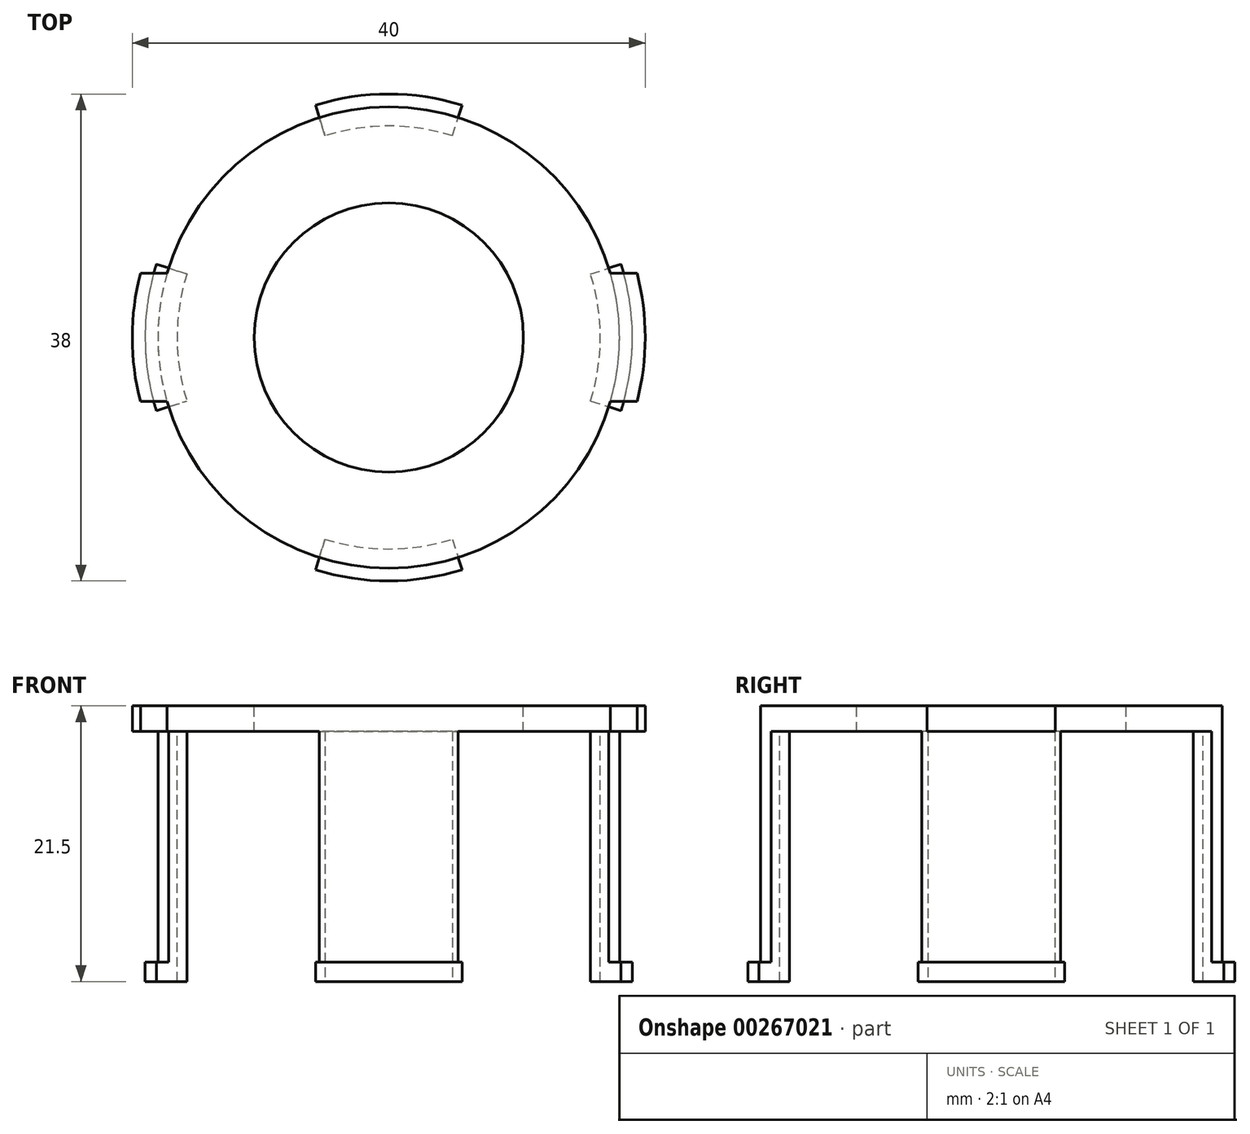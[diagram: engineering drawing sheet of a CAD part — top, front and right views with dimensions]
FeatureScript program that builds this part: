
annotation { "Feature Type Name" : "Feature", "Feature Type Description" : "" }
export const myFeature = defineFeature(function(context is Context, id is Id, definition is map)
    precondition{}
    {
        {
            var Q0;
            Q0=qCreatedBy(makeId("Top.planeOp"),FACE);
            var sketch = newSketch(context, id + "F0", { "sketchPlane" : qUnion([Q0])});
            skCircle(sketch, "E0", {"center": v(0, 0) * mm, "radius": 16.5 * mm});
            skCircle(sketch, "E1", {"center": v(0, 0) * mm, "radius": 18 * mm});
            skSolve(sketch);
        }
        {
            var Q0;
            Q0 = qSketchRegion(id + "F0", true);
            extrude(context, id + "F1", {"entities" : qUnion([Q0]), "oppositeDirection" : true, "depth" : 20 * mm});
        }
        {
            var Q0;
            Q0=makeQuery(id+"F1.opExtrude","CAP_FACE",FACE,{"disambiguationData":[OSD([sQuery(id+"F0.wireOp",EDGE,"E0"),sQuery(id+"F0.wireOp",EDGE,"E1")])],"isStart":false});
            var sketch = newSketch(context, id + "F2", { "sketchPlane" : qUnion([Q0])});
            skLineSegment(sketch, "E2", {"start": v(-17.17, 5.41) * mm, "end": v(-15.74, 4.96) * mm});
            skLineSegment(sketch, "E3", {"start": v(-17.17, -5.41) * mm, "end": v(-15.74, -4.96) * mm});
            skLineSegment(sketch, "E4", {"start": v(-5.41, 17.17) * mm, "end": v(-4.96, 15.74) * mm});
            skLineSegment(sketch, "E5", {"start": v(-5.41, -17.17) * mm, "end": v(-4.96, -15.74) * mm});
            skArc(sketch, "E6", {"start": v(-17.17, -5.41) * mm, "mid": v(-12.73, -12.73) * mm, "end": v(-5.41, -17.17) * mm});
            skArc(sketch, "E7", {"start": v(-15.74, -4.96) * mm, "mid": v(-11.67, -11.67) * mm, "end": v(-4.96, -15.74) * mm});
            skLineSegment(sketch, "E8.trimOffspring", {"start": v(4.96, -15.74) * mm, "end": v(5.41, -17.17) * mm});
            skLineSegment(sketch, "E9.trimOffspring", {"start": v(4.96, 15.74) * mm, "end": v(5.41, 17.17) * mm});
            skLineSegment(sketch, "E10.trimOffspring", {"start": v(15.74, 4.96) * mm, "end": v(17.17, 5.41) * mm});
            skLineSegment(sketch, "E11.trimOffspring", {"start": v(15.74, -4.96) * mm, "end": v(17.17, -5.41) * mm});
            skArc(sketch, "E12.trimOffspring", {"start": v(5.41, -17.17) * mm, "mid": v(12.73, -12.73) * mm, "end": v(17.17, -5.41) * mm});
            skArc(sketch, "E13.trimOffspring", {"start": v(4.96, -15.74) * mm, "mid": v(11.67, -11.67) * mm, "end": v(15.74, -4.96) * mm});
            skArc(sketch, "E14.trimOffspring", {"start": v(15.74, 4.96) * mm, "mid": v(11.67, 11.67) * mm, "end": v(4.96, 15.74) * mm});
            skArc(sketch, "E15.trimOffspring", {"start": v(17.17, 5.41) * mm, "mid": v(12.73, 12.73) * mm, "end": v(5.41, 17.17) * mm});
            skArc(sketch, "E16.trimOffspring", {"start": v(-5.41, 17.17) * mm, "mid": v(-12.73, 12.73) * mm, "end": v(-17.17, 5.41) * mm});
            skArc(sketch, "E17.trimOffspring", {"start": v(-4.96, 15.74) * mm, "mid": v(-11.67, 11.67) * mm, "end": v(-15.74, 4.96) * mm});
            skSolve(sketch);
        }
        {
            var Q0;
            Q0 = qSketchRegion(id + "F2", true);
            extrude(context, id + "F3", {"entities" : qUnion([Q0]), "operationType" : NewBodyOperationType.REMOVE, "oppositeDirection" : true, "depth" : 18 * mm});
        }
        {
            var Q0;
            {var subQ0=sQuery(id+"F0.wireOp",EDGE,"E0");var subQ1=sQuery(id+"F0.wireOp",EDGE,"E1");Q0=makeQuery(id+"F3.boolean.opBoolean","SPLIT",FACE,{"disambiguationData":[TD([makeQuery(id+"F3.opExtrude","SWEPT_FACE",FACE,{"disambiguationData":[OSD([sQuery(id+"F2.wireOp",EDGE,"E10.trimOffspring")])]})])],"derivedFrom":makeQuery(id+"F1.opExtrude","CAP_FACE",FACE,{"disambiguationData":[OSD([subQ0,subQ1])],"isStart":false})});}
            var sketch = newSketch(context, id + "F4", { "sketchPlane" : qUnion([Q0])});
            skArc(sketch, "E18", {"start": v(-17.17, 5.41) * mm, "mid": v(-18, 0) * mm, "end": v(-17.17, -5.41) * mm});
            skArc(sketch, "E19", {"start": v(-15.74, 4.96) * mm, "mid": v(-16.5, 0) * mm, "end": v(-15.74, -4.96) * mm});
            skLineSegment(sketch, "E20", {"start": v(-18.12, 5.71) * mm, "end": v(-15.74, 4.96) * mm});
            skLineSegment(sketch, "E21", {"start": v(-15.74, -4.96) * mm, "end": v(-18.12, -5.71) * mm});
            skLineSegment(sketch, "E22", {"start": v(-4.96, -15.74) * mm, "end": v(-5.71, -18.12) * mm});
            skLineSegment(sketch, "E23", {"start": v(4.96, -15.74) * mm, "end": v(5.71, -18.12) * mm});
            skLineSegment(sketch, "E24", {"start": v(15.74, -4.96) * mm, "end": v(18.12, -5.71) * mm});
            skLineSegment(sketch, "E25", {"start": v(15.74, 4.96) * mm, "end": v(18.12, 5.71) * mm});
            skLineSegment(sketch, "E26", {"start": v(4.96, 15.74) * mm, "end": v(5.71, 18.12) * mm});
            skLineSegment(sketch, "E27", {"start": v(-4.96, 15.74) * mm, "end": v(-5.71, 18.12) * mm});
            skArc(sketch, "E28", {"start": v(-18.12, 5.71) * mm, "mid": v(-19, 0) * mm, "end": v(-18.12, -5.71) * mm});
            skArc(sketch, "E29.trimOffspring", {"start": v(5.71, 18.12) * mm, "mid": v(0, 19) * mm, "end": v(-5.71, 18.12) * mm});
            skArc(sketch, "E30.trimOffspring", {"start": v(5.41, 17.17) * mm, "mid": v(0, 18) * mm, "end": v(-5.41, 17.17) * mm});
            skArc(sketch, "E31.trimOffspring", {"start": v(4.96, 15.74) * mm, "mid": v(0, 16.5) * mm, "end": v(-4.96, 15.74) * mm});
            skArc(sketch, "E32.trimOffspring", {"start": v(15.74, -4.96) * mm, "mid": v(16.5, 0) * mm, "end": v(15.74, 4.96) * mm});
            skArc(sketch, "E33.trimOffspring", {"start": v(17.17, -5.41) * mm, "mid": v(18, 0) * mm, "end": v(17.17, 5.41) * mm});
            skArc(sketch, "E34.trimOffspring", {"start": v(18.12, -5.71) * mm, "mid": v(19, 0) * mm, "end": v(18.12, 5.71) * mm});
            skArc(sketch, "E35.trimOffspring", {"start": v(-5.71, -18.12) * mm, "mid": v(0, -19) * mm, "end": v(5.71, -18.12) * mm});
            skArc(sketch, "E36.trimOffspring", {"start": v(-5.41, -17.17) * mm, "mid": v(0, -18) * mm, "end": v(5.41, -17.17) * mm});
            skArc(sketch, "E37.trimOffspring", {"start": v(-4.96, -15.74) * mm, "mid": v(0, -16.5) * mm, "end": v(4.96, -15.74) * mm});
            skSolve(sketch);
        }
        {
            var Q0;
            Q0 = qSketchRegion(id + "F4", true);
            extrude(context, id + "F5", {"entities" : qUnion([Q0]), "operationType" : NewBodyOperationType.ADD, "depth" : 1.5 * mm});
        }
        {
            var Q0;
            Q0=makeQuery(id+"F1.opExtrude","CAP_FACE",FACE,{"disambiguationData":[OSD([sQuery(id+"F0.wireOp",EDGE,"E0"),sQuery(id+"F0.wireOp",EDGE,"E1")])],"isStart":true});
            var sketch = newSketch(context, id + "F6", { "sketchPlane" : qUnion([Q0])});
            skSolve(sketch);
        }
        {
            var Q0;
            Q0=makeQuery(id+"F6.imprint","IMPRINT",FACE,{"disambiguationData":[TD([[makeQuery(id+"F6.imprint","IMPRINT",EDGE,{"derivedFrom":makeQuery(id+"F1.opExtrude","CAP_EDGE",EDGE,{"disambiguationData":[OSD([sQuery(id+"F0.wireOp",EDGE,"E0")])],"isStart":true})}),-1.0]])]});
            var sketch = newSketch(context, id + "F7", { "sketchPlane" : qUnion([Q0])});
            skCircle(sketch, "E38", {"center": v(0, 0) * mm, "radius": 10.5 * mm});
            skCircle(sketch, "E39", {"center": v(0, 0) * mm, "radius": 20 * mm});
            skSolve(sketch);
        }
        {
            var Q0;
            Q0 = qSketchRegion(id + "F7", true);
            extrude(context, id + "F8", {"entities" : qUnion([Q0]), "operationType" : NewBodyOperationType.ADD, "oppositeDirection" : true, "depth" : 2 * mm});
        }
        {
            var Q0;
            Q0=makeQuery(id+"F8.boolean.opBoolean","MERGE",FACE,{"derivedFrom":[makeQuery(id+"F1.opExtrude","CAP_FACE",FACE,{"disambiguationData":[OSD([sQuery(id+"F0.wireOp",EDGE,"E0"),sQuery(id+"F0.wireOp",EDGE,"E1")])],"isStart":true}),makeQuery(id+"F8.opExtrude","CAP_FACE",FACE,{"disambiguationData":[OSD([sQuery(id+"F7.wireOp",EDGE,"E38"),sQuery(id+"F7.wireOp",EDGE,"E39")])],"isStart":true})]});
            var sketch = newSketch(context, id + "F9", { "sketchPlane" : qUnion([Q0])});
            skArc(sketch, "E40", {"start": v(19.36, 5) * mm, "mid": v(0, 20) * mm, "end": v(-19.36, 5) * mm});
            skArc(sketch, "E41", {"start": v(17.3, 5) * mm, "mid": v(0, 18) * mm, "end": v(-17.3, 5) * mm});
            skLineSegment(sketch, "E42", {"start": v(-31.22, 0) * mm, "end": v(34.73, 0) * mm, "construction": true});
            skLineSegment(sketch, "E43", {"start": v(-19.36, 5) * mm, "end": v(-17.3, 5) * mm});
            skLineSegment(sketch, "E44", {"start": v(-19.36, -5) * mm, "end": v(-17.3, -5) * mm});
            skLineSegment(sketch, "E45.trimOffspring", {"start": v(17.3, 5) * mm, "end": v(19.36, 5) * mm});
            skLineSegment(sketch, "E46.trimOffspring", {"start": v(17.3, -5) * mm, "end": v(19.36, -5) * mm});
            skArc(sketch, "E47.trimOffspring", {"start": v(-17.3, -5) * mm, "mid": v(0, -18) * mm, "end": v(17.3, -5) * mm});
            skArc(sketch, "E48.trimOffspring", {"start": v(-19.36, -5) * mm, "mid": v(0, -20) * mm, "end": v(19.36, -5) * mm});
            skSolve(sketch);
        }
        {
            var Q0;
            Q0 = qSketchRegion(id + "F9", true);
            extrude(context, id + "F10", {"entities" : qUnion([Q0]), "operationType" : NewBodyOperationType.REMOVE, "oppositeDirection" : true, "depth" : 12.4 * mm});
        }
    });
